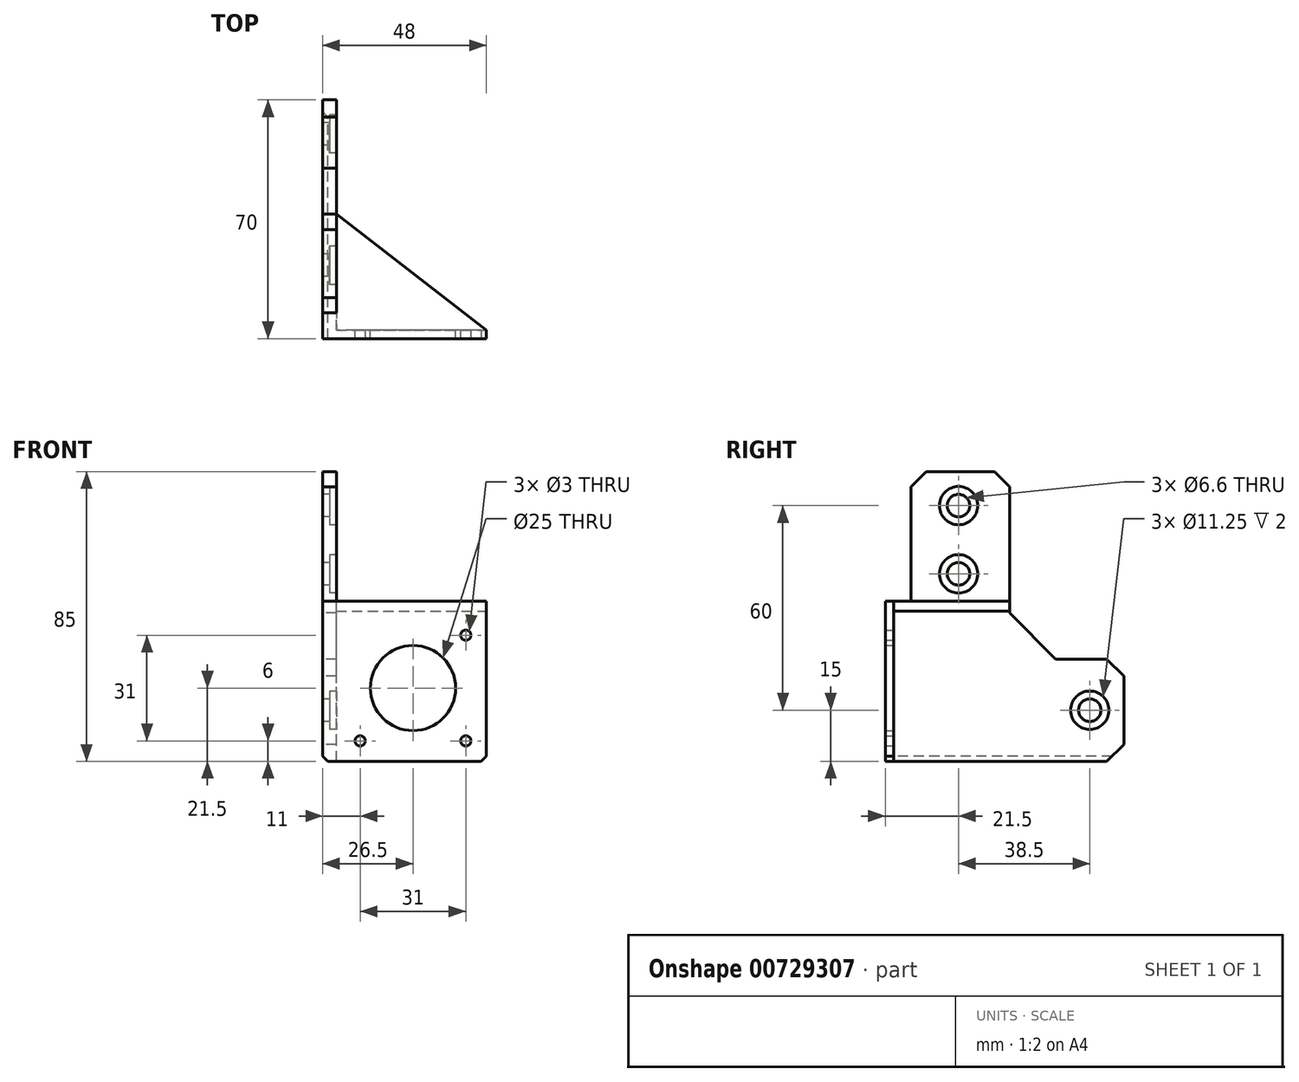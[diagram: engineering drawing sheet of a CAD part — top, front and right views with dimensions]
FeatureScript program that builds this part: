
annotation { "Feature Type Name" : "Feature", "Feature Type Description" : "" }
export const myFeature = defineFeature(function(context is Context, id is Id, definition is map)
    precondition{}
    {
        {
            var Q0;
            Q0=qCreatedBy(makeId("Front.planeOp"),FACE);
            var sketch = newSketch(context, id + "F0", { "sketchPlane" : qUnion([Q0])});
            skLineSegment(sketch, "E0.bottom", {"start": v(0, 0) * mm, "end": v(43, 0) * mm, "construction": true});
            skLineSegment(sketch, "E0.top", {"start": v(0, 43) * mm, "end": v(43, 43) * mm, "construction": true});
            skLineSegment(sketch, "E0.left", {"start": v(0, 0) * mm, "end": v(0, 43) * mm, "construction": true});
            skLineSegment(sketch, "E0.right", {"start": v(43, 0) * mm, "end": v(43, 43) * mm, "construction": true});
            skPoint(sketch, "E0.middle", {"position": v(21.5, 21.5) * mm});
            skLineSegment(sketch, "E1.bottom", {"start": v(6, 6) * mm, "end": v(37, 6) * mm, "construction": true});
            skLineSegment(sketch, "E1.top", {"start": v(6, 37) * mm, "end": v(37, 37) * mm, "construction": true});
            skLineSegment(sketch, "E1.left", {"start": v(6, 6) * mm, "end": v(6, 37) * mm, "construction": true});
            skLineSegment(sketch, "E1.right", {"start": v(37, 6) * mm, "end": v(37, 37) * mm, "construction": true});
            skCircle(sketch, "E2", {"center": v(21.5, 21.5) * mm, "radius": 12.5 * mm, "construction": true});
            skSolve(sketch);
        }
        {
            var Q0;
            Q0=qCreatedBy(makeId("Front.planeOp"),FACE);
            var sketch = newSketch(context, id + "F1", { "sketchPlane" : qUnion([Q0])});
            skLineSegment(sketch, "E3", {"start": v(43, 0) * mm, "end": v(-5, 0) * mm});
            skLineSegment(sketch, "E4", {"start": v(-5, 0) * mm, "end": v(-5, 47) * mm});
            skLineSegment(sketch, "E5", {"start": v(-5, 47) * mm, "end": v(43, 47) * mm});
            skLineSegment(sketch, "E6", {"start": v(43, 47) * mm, "end": v(43, 0) * mm});
            skSolve(sketch);
        }
        {
            var Q0;
            Q0=makeQuery(id+"F1.imprint","IMPRINT",FACE,{"disambiguationData":[TD([[makeQuery(id+"F1.imprint","IMPRINT",EDGE,{"derivedFrom":sQuery(id+"F1.wireOp",EDGE,"E3")}),-1.0]])]});
            extrude(context, id + "F2", {"entities" : qUnion([Q0]), "depth" : 2.5 * mm, "offsetDistance" : 25 * mm});
        }
        {
            var Q0;
            Q0=makeQuery(id+"F2.opExtrude","SWEPT_FACE",FACE,{"disambiguationData":[OSD([sQuery(id+"F1.wireOp",EDGE,"E4")])]});
            var sketch = newSketch(context, id + "F3", { "sketchPlane" : qUnion([Q0])});
            skLineSegment(sketch, "E7", {"start": v(0, 0) * mm, "end": v(-62.5, 0) * mm});
            skLineSegment(sketch, "E8", {"start": v(-62.5, 0) * mm, "end": v(-67.5, 5) * mm});
            skLineSegment(sketch, "E9", {"start": v(-67.5, 5) * mm, "end": v(-67.5, 25) * mm});
            skLineSegment(sketch, "E10", {"start": v(-67.5, 25) * mm, "end": v(-62.5, 30) * mm});
            skLineSegment(sketch, "E11", {"start": v(-62.5, 30) * mm, "end": v(-47.5, 30) * mm});
            skLineSegment(sketch, "E12", {"start": v(-47.5, 30) * mm, "end": v(-34, 43.5) * mm});
            skLineSegment(sketch, "E13", {"start": v(-34, 43.5) * mm, "end": v(-34, 80.5) * mm});
            skLineSegment(sketch, "E14", {"start": v(-34, 80.5) * mm, "end": v(-29.5, 85) * mm});
            skLineSegment(sketch, "E15", {"start": v(-29.5, 85) * mm, "end": v(-9.5, 85) * mm});
            skLineSegment(sketch, "E16", {"start": v(-9.5, 85) * mm, "end": v(-5, 80.5) * mm});
            skLineSegment(sketch, "E17", {"start": v(-5, 80.5) * mm, "end": v(-5, 47) * mm});
            skLineSegment(sketch, "E18", {"start": v(-5, 47) * mm, "end": v(0, 47) * mm});
            skLineSegment(sketch, "E19", {"start": v(0, 47) * mm, "end": v(0, 0) * mm});
            skSolve(sketch);
        }
        {
            var Q0;
            Q0=makeQuery(id+"F3.imprint","IMPRINT",FACE,{"disambiguationData":[TD([[makeQuery(id+"F3.imprint","IMPRINT",EDGE,{"derivedFrom":sQuery(id+"F3.wireOp",EDGE,"E7")}),-1.0]])]});
            extrude(context, id + "F4", {"entities" : qUnion([Q0]), "operationType" : NewBodyOperationType.ADD, "oppositeDirection" : true, "depth" : 4 * mm, "offsetDistance" : 25 * mm});
        }
        {
            var Q0;
            Q0=makeQuery(id+"F4.boolean.opBoolean","MERGE",FACE,{"derivedFrom":[makeQuery(id+"F2.opExtrude","SWEPT_FACE",FACE,{"disambiguationData":[OSD([sQuery(id+"F1.wireOp",EDGE,"E5")])]}),makeQuery(id+"F4.opExtrude","SWEPT_FACE",FACE,{"disambiguationData":[OSD([sQuery(id+"F3.wireOp",EDGE,"E18")])]})]});
            var sketch = newSketch(context, id + "F5", { "sketchPlane" : qUnion([Q0])});
            skLineSegment(sketch, "E20", {"start": v(-1, 0) * mm, "end": v(43, 0) * mm});
            skLineSegment(sketch, "E21", {"start": v(43, 0) * mm, "end": v(-1, 34) * mm});
            skLineSegment(sketch, "E22", {"start": v(-1, 34) * mm, "end": v(-1, 0) * mm});
            skSolve(sketch);
        }
        {
            var Q0;
            {var subQ0=sQuery(id+"F5.wireOp",EDGE,"E20");Q0=makeQuery(id+"F5.imprint","IMPRINT",FACE,{"disambiguationData":[TD([[makeQuery(id+"F5.imprint","IMPRINT",EDGE,{"derivedFrom":subQ0}),1.0]])]});}
            extrude(context, id + "F6", {"entities" : qUnion([Q0]), "operationType" : NewBodyOperationType.ADD, "oppositeDirection" : true, "depth" : 3 * mm, "offsetDistance" : 25 * mm});
        }
        {
            var Q0;
            {var subQ0=sQuery(id+"F3.wireOp",EDGE,"E13");var subQ2=sQuery(id+"F3.wireOp",EDGE,"E12");var subQ3=sQuery(id+"F3.wireOp",EDGE,"E11");var subQ4=sQuery(id+"F3.wireOp",EDGE,"E10");var subQ5=sQuery(id+"F3.wireOp",EDGE,"E9");var subQ6=sQuery(id+"F1.wireOp",EDGE,"E3");var subQ7=sQuery(id+"F3.wireOp",EDGE,"E8");var subQ8=sQuery(id+"F3.wireOp",EDGE,"E7");Q0=makeQuery(id+"F6.boolean.opBoolean","SPLIT",FACE,{"disambiguationData":[TD([makeQuery(id+"F2.opExtrude","SWEPT_FACE",FACE,{"disambiguationData":[OSD([subQ6])]})])],"derivedFrom":makeQuery(id+"F4.opExtrude","CAP_FACE",FACE,{"disambiguationData":[OSD([subQ8,subQ7,subQ5,subQ4,subQ3,subQ2,subQ0,sQuery(id+"F3.wireOp",EDGE,"E14"),sQuery(id+"F3.wireOp",EDGE,"E15"),sQuery(id+"F3.wireOp",EDGE,"E16"),sQuery(id+"F3.wireOp",EDGE,"E17"),sQuery(id+"F3.wireOp",EDGE,"E18"),sQuery(id+"F3.wireOp",EDGE,"E19")])],"isStart":false})});}
            var sketch = newSketch(context, id + "F7", { "sketchPlane" : qUnion([Q0])});
            skPoint(sketch, "E23", {"position": v(57.5, 15) * mm});
            skPoint(sketch, "E23.positionSnap0", {"position": v(55, 30) * mm});
            skPoint(sketch, "E23.positionSnap1", {"position": v(67.5, 15) * mm});
            skPoint(sketch, "E24", {"position": v(19, 75) * mm});
            skPoint(sketch, "E25", {"position": v(19, 55) * mm});
            skSolve(sketch);
        }
        {
            var Q0;
            Q0=sQuery(id+"F7.wireOp",VERTEX,"E24");
            var Q1;
            Q1=sQuery(id+"F7.wireOp",VERTEX,"E25");
            var Q2;
            Q2=sQuery(id+"F7.wireOp",VERTEX,"E23");
            var Q3;
            Q3=makeQuery(id+"F2.opExtrude","SWEPT_BODY",BODY,{"disambiguationData":[OSD([sQuery(id+"F1.wireOp",EDGE,"E3"),sQuery(id+"F1.wireOp",EDGE,"E4"),sQuery(id+"F1.wireOp",EDGE,"E5"),sQuery(id+"F1.wireOp",EDGE,"E6")])]});
            hole(context, id + "F8", {"style" : HoleStyle.C_BORE, "endStyle" : HoleEndStyle.THROUGH, "holeDiameter" : 6.6 * mm, "cBoreDiameter" : 11.25 * mm, "cBoreDepth" : 2 * mm, "majorDiameter" : 5 * mm, "isTappedThrough" : true, "tappedDepth" : 12 * mm, "tapClearance" : 3, "locations" : qUnion([Q0, Q1, Q2]), "scope" : qUnion([Q3])});
        }
        {
            var Q0;
            Q0=makeQuery(id+"F2.opExtrude","CAP_FACE",FACE,{"disambiguationData":[OSD([sQuery(id+"F1.wireOp",EDGE,"E3"),sQuery(id+"F1.wireOp",EDGE,"E4"),sQuery(id+"F1.wireOp",EDGE,"E5"),sQuery(id+"F1.wireOp",EDGE,"E6")])],"isStart":true});
            var sketch = newSketch(context, id + "F9", { "sketchPlane" : qUnion([Q0])});
            skCircle(sketch, "E26", {"center": v(-37, 37) * mm, "radius": 1.5 * mm});
            skCircle(sketch, "E27", {"center": v(-37, 6) * mm, "radius": 1.5 * mm});
            skCircle(sketch, "E28", {"center": v(-6, 6) * mm, "radius": 1.5 * mm});
            skCircle(sketch, "E29", {"center": v(-21.5, 21.5) * mm, "radius": 12.5 * mm});
            skSolve(sketch);
        }
        {
            var Q0;
            Q0 = qSketchRegion(id + "F9", true);
            extrude(context, id + "F10", {"entities" : qUnion([Q0]), "operationType" : NewBodyOperationType.REMOVE, "endBound" : BoundingType.THROUGH_ALL, "oppositeDirection" : true, "depth" : 25 * mm, "offsetDistance" : 25 * mm});
        }
        {
            var Q0;
            Q0=makeQuery(id+"F2.opExtrude","SWEPT_EDGE",EDGE,{"disambiguationData":[OSD([sQuery(id+"F1.wireOp",EDGE,"E3"),sQuery(id+"F1.wireOp",EDGE,"E6")])]});
            var Q1;
            Q1=makeQuery(id+"F4.boolean.opBoolean","MERGE",EDGE,{"derivedFrom":[makeQuery(id+"F2.opExtrude","SWEPT_EDGE",EDGE,{"disambiguationData":[OSD([sQuery(id+"F1.wireOp",EDGE,"E3"),sQuery(id+"F1.wireOp",EDGE,"E4")])]}),makeQuery(id+"F4.opExtrude","CAP_EDGE",EDGE,{"disambiguationData":[OSD([sQuery(id+"F3.wireOp",EDGE,"E7")])],"isStart":true})]});
            chamfer(context, id + "F11", {"entities" : qUnion([Q0, Q1]), "width" : 1.5 * mm, "tangentPropagation" : true});
        }
    });
